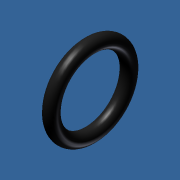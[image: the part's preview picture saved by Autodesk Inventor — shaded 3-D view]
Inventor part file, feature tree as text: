
AUTODESK INVENTOR PART (.ipt)
format: ipt  version: unknown  size: 193,024 bytes
history: native  units: in
note: dims shown in document units (in); Inventor stores cm internally (conversion verified against a paired STEP export)
features: revolve x1, sketch x1
ambient origin geometry x8: Origin, YZ Plane, XZ Plane, XY Plane, X Axis, Y Axis, Z Axis, Center Point
bodies: Solid1 (feature_tree)
feature tree (2):
  revolve  "Revolution1"  [1 undecoded]
  sketch  "Sketch1"  dims[d0=0.125in d1=0.3045in d2=90.0deg]
note: 1 required parameter value undecoded (feature->parameter linkage not recoverable at this tier; creation-order binding heuristic only, values carry confidence <= 0.55)
